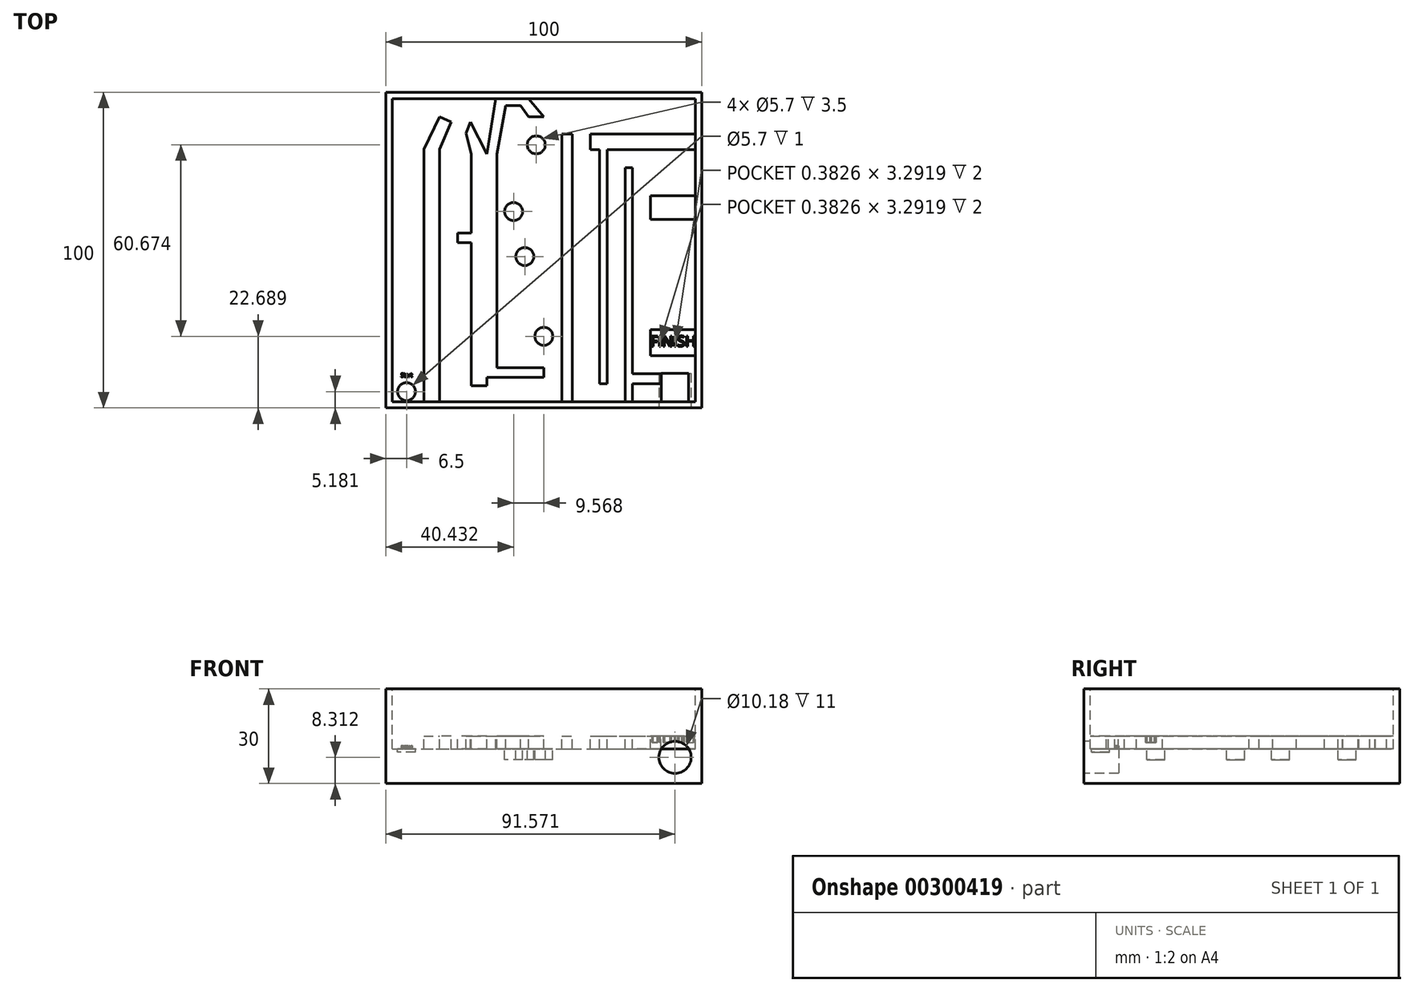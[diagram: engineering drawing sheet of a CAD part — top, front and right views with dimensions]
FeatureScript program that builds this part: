
annotation { "Feature Type Name" : "Feature", "Feature Type Description" : "" }
export const myFeature = defineFeature(function(context is Context, id is Id, definition is map)
    precondition{}
    {
        {
            var Q0;
            Q0=qCreatedBy(makeId("Top.planeOp"),FACE);
            var sketch = newSketch(context, id + "F0", { "sketchPlane" : qUnion([Q0])});
            skLineSegment(sketch, "E0.bottom", {"start": v(-50, 50) * mm, "end": v(50, 50) * mm});
            skLineSegment(sketch, "E0.top", {"start": v(-50, -50) * mm, "end": v(50, -50) * mm});
            skLineSegment(sketch, "E0.left", {"start": v(-50, 50) * mm, "end": v(-50, -50) * mm});
            skLineSegment(sketch, "E0.right", {"start": v(50, 50) * mm, "end": v(50, -50) * mm});
            skPoint(sketch, "E0.middle", {"position": v(0, 0) * mm});
            skSolve(sketch);
        }
        {
            var Q0;
            Q0 = qSketchRegion(id + "F0", true);
            extrude(context, id + "F1", {"entities" : qUnion([Q0]), "depth" : 30 * mm});
        }
        {
            var Q0;
            Q0=makeQuery(id+"F1.opExtrude","CAP_FACE",FACE,{"disambiguationData":[OSD([sQuery(id+"F0.wireOp",EDGE,"E0.bottom"),sQuery(id+"F0.wireOp",EDGE,"E0.top"),sQuery(id+"F0.wireOp",EDGE,"E0.left"),sQuery(id+"F0.wireOp",EDGE,"E0.right")])],"isStart":false});
            var sketch = newSketch(context, id + "F2", { "sketchPlane" : qUnion([Q0])});
            skLineSegment(sketch, "E1.bottom", {"start": v(-48, 48) * mm, "end": v(48, 48) * mm});
            skLineSegment(sketch, "E1.top", {"start": v(-48, -48) * mm, "end": v(48, -48) * mm});
            skLineSegment(sketch, "E1.left", {"start": v(-48, 48) * mm, "end": v(-48, -48) * mm});
            skLineSegment(sketch, "E1.right", {"start": v(48, 48) * mm, "end": v(48, -48) * mm});
            skPoint(sketch, "E1.middle", {"position": v(0, 0) * mm});
            skSolve(sketch);
        }
        {
            var Q0;
            Q0 = qSketchRegion(id + "F2", true);
            extrude(context, id + "F3", {"entities" : qUnion([Q0]), "operationType" : NewBodyOperationType.REMOVE, "oppositeDirection" : true, "depth" : 15 * mm});
        }
        {
            var Q0;
            Q0=makeQuery(id+"F3.boolean.opBoolean","COPY",FACE,{"derivedFrom":makeQuery(id+"F3.opExtrude","CAP_FACE",FACE,{"disambiguationData":[OSD([sQuery(id+"F2.wireOp",EDGE,"E1.bottom"),sQuery(id+"F2.wireOp",EDGE,"E1.top"),sQuery(id+"F2.wireOp",EDGE,"E1.left"),sQuery(id+"F2.wireOp",EDGE,"E1.right")])],"isStart":false})});
            var sketch = newSketch(context, id + "F4", { "sketchPlane" : qUnion([Q0])});
            skLineSegment(sketch, "E2.bottom", {"start": v(-38, -48) * mm, "end": v(-33, -48) * mm});
            skLineSegment(sketch, "E2.top", {"start": v(-38, 32) * mm, "end": v(-33, 32) * mm});
            skLineSegment(sketch, "E2.left", {"start": v(-38, -48) * mm, "end": v(-38, 32) * mm});
            skLineSegment(sketch, "E2.right", {"start": v(-33, -48) * mm, "end": v(-33, 32) * mm});
            skLineSegment(sketch, "E3", {"start": v(-38, 32) * mm, "end": v(-33, 42.3) * mm});
            skLineSegment(sketch, "E4", {"start": v(-33, 42.3) * mm, "end": v(-29.38, 40.54) * mm});
            skLineSegment(sketch, "E5", {"start": v(-29.38, 40.54) * mm, "end": v(-33, 32) * mm});
            skLineSegment(sketch, "E6.bottom", {"start": v(-23, -43) * mm, "end": v(-18, -43) * mm});
            skLineSegment(sketch, "E6.top", {"start": v(-23, 30.5) * mm, "end": v(-18, 30.5) * mm});
            skLineSegment(sketch, "E6.left", {"start": v(-23, -43) * mm, "end": v(-23, 30.5) * mm});
            skLineSegment(sketch, "E6.right", {"start": v(-18, -43) * mm, "end": v(-18, 30.5) * mm});
            skLineSegment(sketch, "E7.bottom", {"start": v(-23, 5.39) * mm, "end": v(-27.3, 5.39) * mm});
            skLineSegment(sketch, "E7.top", {"start": v(-23, 2.3) * mm, "end": v(-27.3, 2.3) * mm});
            skLineSegment(sketch, "E7.left", {"start": v(-23, 5.39) * mm, "end": v(-23, 2.3) * mm});
            skLineSegment(sketch, "E7.right", {"start": v(-27.3, 5.39) * mm, "end": v(-27.3, 2.3) * mm});
            skLineSegment(sketch, "E8", {"start": v(-23.19, 40.54) * mm, "end": v(-24.65, 37.1) * mm});
            skLineSegment(sketch, "E9", {"start": v(-24.65, 37.1) * mm, "end": v(-23, 30.5) * mm});
            skLineSegment(sketch, "E10", {"start": v(-18, 30.5) * mm, "end": v(-23.19, 40.54) * mm});
            skLineSegment(sketch, "E11", {"start": v(-18, 30.5) * mm, "end": v(-15.3, 48) * mm});
            skLineSegment(sketch, "E12", {"start": v(-15.3, 48) * mm, "end": v(-4.87, 48) * mm});
            skLineSegment(sketch, "E13", {"start": v(-4.87, 48) * mm, "end": v(0, 42.2) * mm});
            skLineSegment(sketch, "E14", {"start": v(0, 42.2) * mm, "end": v(-4.87, 42.2) * mm});
            skLineSegment(sketch, "E15", {"start": v(-4.87, 42.2) * mm, "end": v(-7.38, 45.78) * mm});
            skLineSegment(sketch, "E16", {"start": v(-7.38, 45.78) * mm, "end": v(-12.09, 45.78) * mm});
            skLineSegment(sketch, "E17", {"start": v(-12.09, 45.78) * mm, "end": v(-14.8, 30.5) * mm});
            skLineSegment(sketch, "E18", {"start": v(-14.8, -40.3) * mm, "end": v(0, -40.3) * mm});
            skLineSegment(sketch, "E19", {"start": v(0, -40.3) * mm, "end": v(0, -37.3) * mm});
            skLineSegment(sketch, "E20", {"start": v(0, -37.3) * mm, "end": v(-12.09, -37.3) * mm});
            skLineSegment(sketch, "E21", {"start": v(-12.09, -37.3) * mm, "end": v(-14.8, -37.3) * mm});
            skLineSegment(sketch, "E22", {"start": v(-14.8, 30.5) * mm, "end": v(-14.8, -37.3) * mm});
            skLineSegment(sketch, "E23", {"start": v(-14.8, -40.3) * mm, "end": v(-18, -40.3) * mm});
            skLineSegment(sketch, "E24.bottom", {"start": v(5.7, -48) * mm, "end": v(6.73, -48) * mm});
            skLineSegment(sketch, "E24.left", {"start": v(5.7, -48) * mm, "end": v(5.7, 36.84) * mm});
            skLineSegment(sketch, "E25", {"start": v(5.7, 36.84) * mm, "end": v(8.98, 36.84) * mm});
            skLineSegment(sketch, "E26", {"start": v(8.98, 36.84) * mm, "end": v(8.98, -48) * mm});
            skPoint(sketch, "E26.endSnap0", {"position": v(0, -48) * mm});
            skLineSegment(sketch, "E27", {"start": v(14.68, 36.84) * mm, "end": v(14.68, 31.88) * mm});
            skLineSegment(sketch, "E28", {"start": v(14.68, 36.84) * mm, "end": v(23.25, 36.84) * mm});
            skLineSegment(sketch, "E29", {"start": v(14.68, 31.88) * mm, "end": v(17.65, 31.88) * mm});
            skLineSegment(sketch, "E30", {"start": v(17.65, 31.88) * mm, "end": v(17.65, -42.3) * mm});
            skLineSegment(sketch, "E31", {"start": v(23.25, 31.88) * mm, "end": v(20.1, 31.88) * mm});
            skLineSegment(sketch, "E32", {"start": v(20.1, 31.88) * mm, "end": v(20.1, -42.3) * mm});
            skLineSegment(sketch, "E33", {"start": v(17.65, -42.3) * mm, "end": v(20.1, -42.3) * mm});
            skLineSegment(sketch, "E34", {"start": v(23.25, 36.84) * mm, "end": v(48, 36.84) * mm});
            skLineSegment(sketch, "E35", {"start": v(23.25, 31.88) * mm, "end": v(48, 31.88) * mm});
            skLineSegment(sketch, "E36", {"start": v(25.8, -48) * mm, "end": v(25.8, 26.18) * mm});
            skLineSegment(sketch, "E37", {"start": v(25.8, 26.18) * mm, "end": v(28.08, 26.18) * mm});
            skLineSegment(sketch, "E38", {"start": v(28.08, 26.18) * mm, "end": v(28.08, -48) * mm});
            skLineSegment(sketch, "E39", {"start": v(28.08, -42.3) * mm, "end": v(37.1, -42.3) * mm});
            skLineSegment(sketch, "E40", {"start": v(48, 17.22) * mm, "end": v(33.78, 17.22) * mm});
            skLineSegment(sketch, "E41", {"start": v(33.78, 17.22) * mm, "end": v(33.78, 9.76) * mm});
            skLineSegment(sketch, "E42", {"start": v(33.78, 9.76) * mm, "end": v(48, 9.76) * mm});
            skLineSegment(sketch, "E43", {"start": v(37.1, -42.3) * mm, "end": v(37.1, -39.11) * mm});
            skLineSegment(sketch, "E44", {"start": v(37.1, -39.11) * mm, "end": v(28.08, -39.11) * mm});
            skLineSegment(sketch, "E45", {"start": v(48, -33.41) * mm, "end": v(33.78, -33.41) * mm});
            skLineSegment(sketch, "E46", {"start": v(33.78, -33.41) * mm, "end": v(33.78, -25.15) * mm});
            skLineSegment(sketch, "E47", {"start": v(33.78, -25.15) * mm, "end": v(48, -25.15) * mm});
            skCircle(sketch, "E48", {"center": v(-9.57, 12.24) * mm, "radius": 2.85 * mm});
            skCircle(sketch, "E49", {"center": v(-6.01, -2.03) * mm, "radius": 2.85 * mm});
            skCircle(sketch, "E50", {"center": v(0, -27.31) * mm, "radius": 2.85 * mm});
            skCircle(sketch, "E51", {"center": v(-2.4, 33.36) * mm, "radius": 2.85 * mm});
            skCircle(sketch, "E52", {"center": v(41.86, -43.14) * mm, "radius": 3.68 * mm});
            skSolve(sketch);
        }
        {
            var Q0;
            {var subQ16=sQuery(id+"F4.wireOp",EDGE,"E2.left");Q0=makeQuery(id+"F4.imprint","IMPRINT",FACE,{"disambiguationData":[TD([[makeQuery(id+"F4.imprint","IMPRINT",EDGE,{"derivedFrom":subQ16}),1.0]])]});}
            extrude(context, id + "F5", {"entities" : qUnion([Q0]), "operationType" : NewBodyOperationType.REMOVE, "oppositeDirection" : true, "depth" : 4 * mm});
        }
        {
            var Q0;
            Q0=makeQuery(id+"F5.boolean.opBoolean","SPLIT",FACE,{"disambiguationData":[TD([makeQuery(id+"F5.opExtrude","SWEPT_FACE",FACE,{"disambiguationData":[OSD([sQuery(id+"F4.wireOp",EDGE,"E52")])]})])],"derivedFrom":makeQuery(id+"F3.boolean.opBoolean","COPY",FACE,{"derivedFrom":makeQuery(id+"F3.opExtrude","CAP_FACE",FACE,{"disambiguationData":[OSD([sQuery(id+"F2.wireOp",EDGE,"E1.bottom"),sQuery(id+"F2.wireOp",EDGE,"E1.top"),sQuery(id+"F2.wireOp",EDGE,"E1.left"),sQuery(id+"F2.wireOp",EDGE,"E1.right")])],"isStart":false})})});
            extrude(context, id + "F6", {"entities" : qUnion([Q0]), "operationType" : NewBodyOperationType.REMOVE, "oppositeDirection" : true, "depth" : 7.5 * mm});
        }
        {
            var Q0;
            Q0=makeQuery(id+"F2.imprint","IMPRINT",FACE,{"disambiguationData":[TD([[makeQuery(id+"F2.imprint","IMPRINT",EDGE,{"derivedFrom":sQuery(id+"F2.wireOp",EDGE,"E1.bottom")}),-1.0]])]});
            var Q1;
            Q1=makeQuery(id+"F5.boolean.opBoolean","SPLIT",FACE,{"disambiguationData":[TD([makeQuery(id+"F5.opExtrude","SWEPT_FACE",FACE,{"disambiguationData":[OSD([sQuery(id+"F4.wireOp",EDGE,"E51")])]})])],"derivedFrom":makeQuery(id+"F3.boolean.opBoolean","COPY",FACE,{"derivedFrom":makeQuery(id+"F3.opExtrude","CAP_FACE",FACE,{"disambiguationData":[OSD([sQuery(id+"F2.wireOp",EDGE,"E1.bottom"),sQuery(id+"F2.wireOp",EDGE,"E1.top"),sQuery(id+"F2.wireOp",EDGE,"E1.left"),sQuery(id+"F2.wireOp",EDGE,"E1.right")])],"isStart":false})})});
            extrude(context, id + "F7", {"entities" : qUnion([Q0, Q1]), "operationType" : NewBodyOperationType.REMOVE, "oppositeDirection" : true, "depth" : 7.5 * mm});
        }
        {
            var Q0;
            Q0=makeQuery(id+"F5.boolean.opBoolean","SPLIT",FACE,{"disambiguationData":[TD([makeQuery(id+"F5.opExtrude","SWEPT_FACE",FACE,{"disambiguationData":[OSD([sQuery(id+"F4.wireOp",EDGE,"E48")])]})])],"derivedFrom":makeQuery(id+"F3.boolean.opBoolean","COPY",FACE,{"derivedFrom":makeQuery(id+"F3.opExtrude","CAP_FACE",FACE,{"disambiguationData":[OSD([sQuery(id+"F2.wireOp",EDGE,"E1.bottom"),sQuery(id+"F2.wireOp",EDGE,"E1.top"),sQuery(id+"F2.wireOp",EDGE,"E1.left"),sQuery(id+"F2.wireOp",EDGE,"E1.right")])],"isStart":false})})});
            extrude(context, id + "F8", {"entities" : qUnion([Q0]), "operationType" : NewBodyOperationType.REMOVE, "oppositeDirection" : true, "depth" : 7.5 * mm});
        }
        {
            var Q0;
            Q0=makeQuery(id+"F5.boolean.opBoolean","SPLIT",FACE,{"disambiguationData":[TD([makeQuery(id+"F5.opExtrude","SWEPT_FACE",FACE,{"disambiguationData":[OSD([sQuery(id+"F4.wireOp",EDGE,"E49")])]})])],"derivedFrom":makeQuery(id+"F3.boolean.opBoolean","COPY",FACE,{"derivedFrom":makeQuery(id+"F3.opExtrude","CAP_FACE",FACE,{"disambiguationData":[OSD([sQuery(id+"F2.wireOp",EDGE,"E1.bottom"),sQuery(id+"F2.wireOp",EDGE,"E1.top"),sQuery(id+"F2.wireOp",EDGE,"E1.left"),sQuery(id+"F2.wireOp",EDGE,"E1.right")])],"isStart":false})})});
            var Q1;
            Q1=makeQuery(id+"F5.boolean.opBoolean","SPLIT",FACE,{"disambiguationData":[TD([makeQuery(id+"F5.opExtrude","SWEPT_FACE",FACE,{"disambiguationData":[OSD([sQuery(id+"F4.wireOp",EDGE,"E50")])]})])],"derivedFrom":makeQuery(id+"F3.boolean.opBoolean","COPY",FACE,{"derivedFrom":makeQuery(id+"F3.opExtrude","CAP_FACE",FACE,{"disambiguationData":[OSD([sQuery(id+"F2.wireOp",EDGE,"E1.bottom"),sQuery(id+"F2.wireOp",EDGE,"E1.top"),sQuery(id+"F2.wireOp",EDGE,"E1.left"),sQuery(id+"F2.wireOp",EDGE,"E1.right")])],"isStart":false})})});
            extrude(context, id + "F9", {"entities" : qUnion([Q0, Q1]), "operationType" : NewBodyOperationType.REMOVE, "oppositeDirection" : true, "depth" : 7.5 * mm});
        }
        {
            var Q0;
            Q0=makeQuery(id+"F1.opExtrude","SWEPT_FACE",FACE,{"disambiguationData":[OSD([sQuery(id+"F0.wireOp",EDGE,"E0.top")])]});
            var sketch = newSketch(context, id + "F10", { "sketchPlane" : qUnion([Q0])});
            skCircle(sketch, "E53", {"center": v(41.57, 8.31) * mm, "radius": 5.09 * mm});
            skSolve(sketch);
        }
        {
            var Q0;
            Q0=makeQuery(id+"F10.imprint","IMPRINT",FACE,{"disambiguationData":[TD([[makeQuery(id+"F10.imprint","IMPRINT",EDGE,{"derivedFrom":sQuery(id+"F10.wireOp",EDGE,"E53")}),1.0]])]});
            extrude(context, id + "F11", {"entities" : qUnion([Q0]), "operationType" : NewBodyOperationType.REMOVE, "oppositeDirection" : true, "depth" : 11 * mm});
        }
        {
            var Q0;
            {var subQ0=sQuery(id+"F4.wireOp",EDGE,"E45");var subQ2=sQuery(id+"F2.wireOp",EDGE,"E1.right");var subQ4=sQuery(id+"F2.wireOp",EDGE,"E1.bottom");var subQ5=sQuery(id+"F2.wireOp",EDGE,"E1.top");Q0=makeQuery(id+"F5.boolean.opBoolean","SPLIT",FACE,{"disambiguationData":[TD([makeQuery(id+"F5.opExtrude","SWEPT_FACE",FACE,{"disambiguationData":[OSD([subQ0])]})])],"derivedFrom":makeQuery(id+"F3.boolean.opBoolean","COPY",FACE,{"derivedFrom":makeQuery(id+"F3.opExtrude","CAP_FACE",FACE,{"disambiguationData":[OSD([subQ4,subQ5,sQuery(id+"F2.wireOp",EDGE,"E1.left"),subQ2])],"isStart":false})})});}
            var sketch = newSketch(context, id + "F12", { "sketchPlane" : qUnion([Q0])});
            skText(sketch, "E54", { "text": "FINISH", "fontName": "OpenSans-Regular.ttf"});
            skPoint(sketch, "E55", {"position": v(33.78, -28.82) * mm});
            const initialGuessF12  = {"E54": [0.03378, -0.03048, 1, 0, 0.00332]};
            skSetInitialGuess(sketch, initialGuessF12);
            skSolve(sketch);
        }
        {
            var Q0;
            Q0 = qSketchRegion(id + "F12", true);
            extrude(context, id + "F13", {"entities" : qUnion([Q0]), "operationType" : NewBodyOperationType.REMOVE, "oppositeDirection" : true, "depth" : 2 * mm});
        }
        {
            var Q0;
            Q0=makeQuery(id+"F5.boolean.opBoolean","COPY",FACE,{"derivedFrom":makeQuery(id+"F5.opExtrude","CAP_FACE",FACE,{"disambiguationData":[OSD([sQuery(id+"F2.wireOp",EDGE,"E1.bottom"),sQuery(id+"F2.wireOp",EDGE,"E1.top"),sQuery(id+"F2.wireOp",EDGE,"E1.left"),sQuery(id+"F2.wireOp",EDGE,"E1.right"),sQuery(id+"F4.wireOp",EDGE,"E2.left"),sQuery(id+"F4.wireOp",EDGE,"E2.right"),sQuery(id+"F4.wireOp",EDGE,"E3"),sQuery(id+"F4.wireOp",EDGE,"E4"),sQuery(id+"F4.wireOp",EDGE,"E5"),sQuery(id+"F4.wireOp",EDGE,"E6.bottom"),sQuery(id+"F4.wireOp",EDGE,"E6.left"),sQuery(id+"F4.wireOp",EDGE,"E6.right"),sQuery(id+"F4.wireOp",EDGE,"E7.bottom"),sQuery(id+"F4.wireOp",EDGE,"E7.top"),sQuery(id+"F4.wireOp",EDGE,"E7.right"),sQuery(id+"F4.wireOp",EDGE,"E8"),sQuery(id+"F4.wireOp",EDGE,"E9"),sQuery(id+"F4.wireOp",EDGE,"E10"),sQuery(id+"F4.wireOp",EDGE,"E11"),sQuery(id+"F4.wireOp",EDGE,"E13"),sQuery(id+"F4.wireOp",EDGE,"E14"),sQuery(id+"F4.wireOp",EDGE,"E15"),sQuery(id+"F4.wireOp",EDGE,"E16"),sQuery(id+"F4.wireOp",EDGE,"E17"),sQuery(id+"F4.wireOp",EDGE,"E18"),sQuery(id+"F4.wireOp",EDGE,"E19"),sQuery(id+"F4.wireOp",EDGE,"E20"),sQuery(id+"F4.wireOp",EDGE,"E21"),sQuery(id+"F4.wireOp",EDGE,"E22"),sQuery(id+"F4.wireOp",EDGE,"E23"),sQuery(id+"F4.wireOp",EDGE,"E24.left"),sQuery(id+"F4.wireOp",EDGE,"E25"),sQuery(id+"F4.wireOp",EDGE,"E26"),sQuery(id+"F4.wireOp",EDGE,"E27"),sQuery(id+"F4.wireOp",EDGE,"E28"),sQuery(id+"F4.wireOp",EDGE,"E29"),sQuery(id+"F4.wireOp",EDGE,"E30"),sQuery(id+"F4.wireOp",EDGE,"E31"),sQuery(id+"F4.wireOp",EDGE,"E32"),sQuery(id+"F4.wireOp",EDGE,"E33"),sQuery(id+"F4.wireOp",EDGE,"E34"),sQuery(id+"F4.wireOp",EDGE,"E35"),sQuery(id+"F4.wireOp",EDGE,"E36"),sQuery(id+"F4.wireOp",EDGE,"E37"),sQuery(id+"F4.wireOp",EDGE,"E38"),sQuery(id+"F4.wireOp",EDGE,"E39"),sQuery(id+"F4.wireOp",EDGE,"E40"),sQuery(id+"F4.wireOp",EDGE,"E41"),sQuery(id+"F4.wireOp",EDGE,"E42"),sQuery(id+"F4.wireOp",EDGE,"E43"),sQuery(id+"F4.wireOp",EDGE,"E44"),sQuery(id+"F4.wireOp",EDGE,"E45"),sQuery(id+"F4.wireOp",EDGE,"E46"),sQuery(id+"F4.wireOp",EDGE,"E47"),sQuery(id+"F4.wireOp",EDGE,"E48"),sQuery(id+"F4.wireOp",EDGE,"E49"),sQuery(id+"F4.wireOp",EDGE,"E50"),sQuery(id+"F4.wireOp",EDGE,"E51"),sQuery(id+"F4.wireOp",EDGE,"E52")])],"isStart":false})});
            var sketch = newSketch(context, id + "F14", { "sketchPlane" : qUnion([Q0])});
            skCircle(sketch, "E56", {"center": v(-43.5, -44.82) * mm, "radius": 2.85 * mm});
            skSolve(sketch);
        }
        {
            var Q0;
            Q0 = qSketchRegion(id + "F14", true);
            extrude(context, id + "F15", {"entities" : qUnion([Q0]), "operationType" : NewBodyOperationType.REMOVE, "oppositeDirection" : true, "depth" : 1 * mm});
        }
        {
            var Q0;
            Q0=makeQuery(id+"F5.boolean.opBoolean","COPY",FACE,{"derivedFrom":makeQuery(id+"F5.opExtrude","CAP_FACE",FACE,{"disambiguationData":[OSD([sQuery(id+"F2.wireOp",EDGE,"E1.bottom"),sQuery(id+"F2.wireOp",EDGE,"E1.top"),sQuery(id+"F2.wireOp",EDGE,"E1.left"),sQuery(id+"F2.wireOp",EDGE,"E1.right"),sQuery(id+"F4.wireOp",EDGE,"E2.left"),sQuery(id+"F4.wireOp",EDGE,"E2.right"),sQuery(id+"F4.wireOp",EDGE,"E3"),sQuery(id+"F4.wireOp",EDGE,"E4"),sQuery(id+"F4.wireOp",EDGE,"E5"),sQuery(id+"F4.wireOp",EDGE,"E6.bottom"),sQuery(id+"F4.wireOp",EDGE,"E6.left"),sQuery(id+"F4.wireOp",EDGE,"E6.right"),sQuery(id+"F4.wireOp",EDGE,"E7.bottom"),sQuery(id+"F4.wireOp",EDGE,"E7.top"),sQuery(id+"F4.wireOp",EDGE,"E7.right"),sQuery(id+"F4.wireOp",EDGE,"E8"),sQuery(id+"F4.wireOp",EDGE,"E9"),sQuery(id+"F4.wireOp",EDGE,"E10"),sQuery(id+"F4.wireOp",EDGE,"E11"),sQuery(id+"F4.wireOp",EDGE,"E13"),sQuery(id+"F4.wireOp",EDGE,"E14"),sQuery(id+"F4.wireOp",EDGE,"E15"),sQuery(id+"F4.wireOp",EDGE,"E16"),sQuery(id+"F4.wireOp",EDGE,"E17"),sQuery(id+"F4.wireOp",EDGE,"E18"),sQuery(id+"F4.wireOp",EDGE,"E19"),sQuery(id+"F4.wireOp",EDGE,"E20"),sQuery(id+"F4.wireOp",EDGE,"E21"),sQuery(id+"F4.wireOp",EDGE,"E22"),sQuery(id+"F4.wireOp",EDGE,"E23"),sQuery(id+"F4.wireOp",EDGE,"E24.left"),sQuery(id+"F4.wireOp",EDGE,"E25"),sQuery(id+"F4.wireOp",EDGE,"E26"),sQuery(id+"F4.wireOp",EDGE,"E27"),sQuery(id+"F4.wireOp",EDGE,"E28"),sQuery(id+"F4.wireOp",EDGE,"E29"),sQuery(id+"F4.wireOp",EDGE,"E30"),sQuery(id+"F4.wireOp",EDGE,"E31"),sQuery(id+"F4.wireOp",EDGE,"E32"),sQuery(id+"F4.wireOp",EDGE,"E33"),sQuery(id+"F4.wireOp",EDGE,"E34"),sQuery(id+"F4.wireOp",EDGE,"E35"),sQuery(id+"F4.wireOp",EDGE,"E36"),sQuery(id+"F4.wireOp",EDGE,"E37"),sQuery(id+"F4.wireOp",EDGE,"E38"),sQuery(id+"F4.wireOp",EDGE,"E39"),sQuery(id+"F4.wireOp",EDGE,"E40"),sQuery(id+"F4.wireOp",EDGE,"E41"),sQuery(id+"F4.wireOp",EDGE,"E42"),sQuery(id+"F4.wireOp",EDGE,"E43"),sQuery(id+"F4.wireOp",EDGE,"E44"),sQuery(id+"F4.wireOp",EDGE,"E45"),sQuery(id+"F4.wireOp",EDGE,"E46"),sQuery(id+"F4.wireOp",EDGE,"E47"),sQuery(id+"F4.wireOp",EDGE,"E48"),sQuery(id+"F4.wireOp",EDGE,"E49"),sQuery(id+"F4.wireOp",EDGE,"E50"),sQuery(id+"F4.wireOp",EDGE,"E51"),sQuery(id+"F4.wireOp",EDGE,"E52")])],"isStart":false})});
            var sketch = newSketch(context, id + "F16", { "sketchPlane" : qUnion([Q0])});
            skText(sketch, "E57", { "text": "Start", "fontName": "OpenSans-Regular.ttf"});
            const initialGuessF16  = {"E57": [-0.04525, -0.04017, 1, 0, 0.00118]};
            skSetInitialGuess(sketch, initialGuessF16);
            skSolve(sketch);
        }
        {
            var Q0;
            Q0 = qSketchRegion(id + "F16", true);
            extrude(context, id + "F17", {"entities" : qUnion([Q0]), "operationType" : NewBodyOperationType.ADD, "depth" : 1 * mm});
        }
    });
